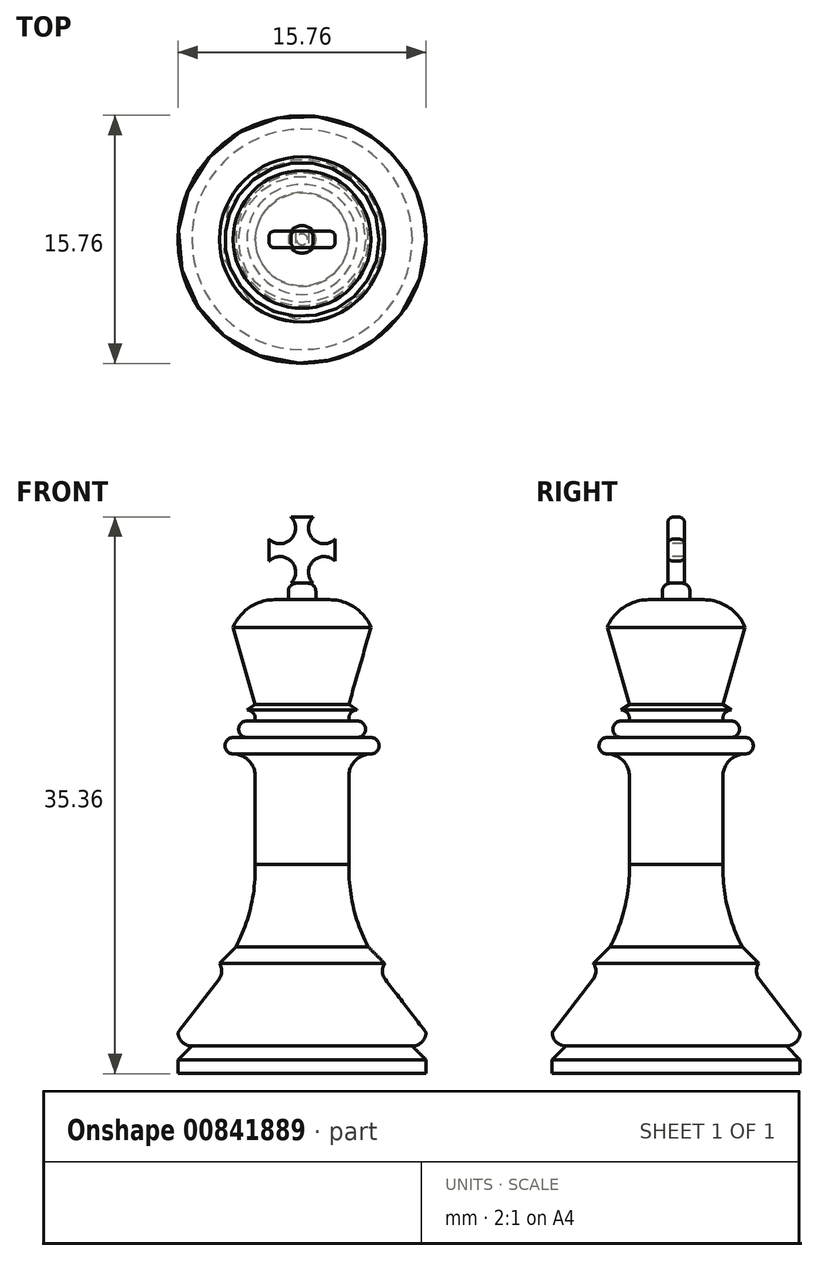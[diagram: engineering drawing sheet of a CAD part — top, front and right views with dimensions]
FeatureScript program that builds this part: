
annotation { "Feature Type Name" : "Feature", "Feature Type Description" : "" }
export const myFeature = defineFeature(function(context is Context, id is Id, definition is map)
    precondition{}
    {
        {
            var Q0;
            Q0=qCreatedBy(makeId("Front.planeOp"),FACE);
            var sketch = newSketch(context, id + "F0", { "sketchPlane" : qUnion([Q0])});
            skLineSegment(sketch, "E0", {"start": v(0, 0) * mm, "end": v(0, 33.5) * mm});
            skLineSegment(sketch, "E1", {"start": v(0, 0) * mm, "end": v(0, -52.5) * mm});
            skLineSegment(sketch, "E2", {"start": v(0, -52.5) * mm, "end": v(-22.5, -52.5) * mm});
            skLineSegment(sketch, "E3", {"start": v(-22.5, -52.5) * mm, "end": v(-22.5, -50) * mm});
            skLineSegment(sketch, "E4", {"start": v(-15, -32.5) * mm, "end": v(-15, -32.5) * mm});
            skLineSegment(sketch, "E5", {"start": v(-22.5, -50) * mm, "end": v(-20, -47.5) * mm});
            skLineSegment(sketch, "E6", {"start": v(-22.5, -45) * mm, "end": v(-22.5, -45) * mm});
            skLineSegment(sketch, "E7", {"start": v(-20, -47.5) * mm, "end": v(-20, -47.5) * mm});
            skPoint(sketch, "E8.visualSharp", {"position": v(-22.5, -47.5) * mm});
            skArc(sketch, "E8.filletArc", {"start": v(-22.47, -45.4) * mm, "mid": v(-21.62, -46.9) * mm, "end": v(-20, -47.5) * mm});
            skLineSegment(sketch, "E9", {"start": v(-15.1, -35.42) * mm, "end": v(-22.3, -44.74) * mm});
            skPoint(sketch, "E10.visualSharp", {"position": v(-22.5, -45) * mm});
            skArc(sketch, "E10.filletArc", {"start": v(-22.3, -44.74) * mm, "mid": v(-22.45, -45.05) * mm, "end": v(-22.47, -45.4) * mm});
            skPoint(sketch, "E11.visualSharp", {"position": v(-14, -34) * mm});
            skArc(sketch, "E11.filletArc", {"start": v(-15.1, -35.42) * mm, "mid": v(-14.58, -33.98) * mm, "end": v(-15, -32.5) * mm});
            skLineSegment(sketch, "E12", {"start": v(-12, -29.5) * mm, "end": v(-15, -32.5) * mm});
            skArc(sketch, "E13", {"start": v(-12, -29.5) * mm, "mid": v(-9.3, -22.22) * mm, "end": v(-8.5, -14.5) * mm});
            skLineSegment(sketch, "E14", {"start": v(-8.5, 1.5) * mm, "end": v(-8.5, -14.5) * mm});
            skLineSegment(sketch, "E15", {"start": v(-12.5, 5.5) * mm, "end": v(-12.5, 5.5) * mm});
            skLineSegment(sketch, "E16", {"start": v(0, 8.5) * mm, "end": v(-12.5, 8.5) * mm});
            skArc(sketch, "E17", {"start": v(-12.5, 8.5) * mm, "mid": v(-14, 7) * mm, "end": v(-12.5, 5.5) * mm});
            skLineSegment(sketch, "E18", {"start": v(-15, -32.5) * mm, "end": v(0, -32.5) * mm});
            skLineSegment(sketch, "E19", {"start": v(-20, -47.5) * mm, "end": v(0, -47.5) * mm});
            skLineSegment(sketch, "E20", {"start": v(0, 8.5) * mm, "end": v(-10, 8.5) * mm});
            skLineSegment(sketch, "E21", {"start": v(-8.5, 11.5) * mm, "end": v(-10, 11.5) * mm});
            skArc(sketch, "E22", {"start": v(-10, 11.5) * mm, "mid": v(-11.5, 10) * mm, "end": v(-10, 8.5) * mm});
            skLineSegment(sketch, "E23", {"start": v(-8.5, 11.5) * mm, "end": v(-8.5, 12) * mm});
            skLineSegment(sketch, "E24", {"start": v(-10, 13.5) * mm, "end": v(-10, 13.5) * mm});
            skLineSegment(sketch, "E25", {"start": v(-10, 13.5) * mm, "end": v(-8.5, 14.5) * mm});
            skLineSegment(sketch, "E26", {"start": v(-8.5, 14.5) * mm, "end": v(0, 14.5) * mm});
            skLineSegment(sketch, "E27", {"start": v(-12.5, 28.5) * mm, "end": v(-8.5, 14.5) * mm});
            skLineSegment(sketch, "E28", {"start": v(0, 33.5) * mm, "end": v(-5, 33.5) * mm});
            skArc(sketch, "E29", {"start": v(-5, 33.5) * mm, "mid": v(-9.5, 32.14) * mm, "end": v(-12.5, 28.5) * mm});
            skPoint(sketch, "E30.newPointB", {"position": v(0, 5.5) * mm});
            skArc(sketch, "E30.filletArc", {"start": v(-8.5, 1.5) * mm, "mid": v(-9.67, 4.33) * mm, "end": v(-12.5, 5.5) * mm});
            skPoint(sketch, "E31.end.orphan", {"position": v(-8.5, 5.5) * mm});
            skPoint(sketch, "E32.visualSharp", {"position": v(-8.5, 13.5) * mm});
            skArc(sketch, "E32.filletArc", {"start": v(-8.5, 12) * mm, "mid": v(-8.94, 13.06) * mm, "end": v(-10, 13.5) * mm});
            skPoint(sketch, "E33.end.orphan", {"position": v(0, 13.5) * mm});
            skSolve(sketch);
        }
        {
            var Q0;
            Q0 = qSketchRegion(id + "F0", true);
            var Q1;
            Q1=sQuery(id+"F0.wireOp",EDGE,"E1");
            revolve(context, id + "F1", {"surfaceOperationType" : NewSurfaceOperationType.NEW, "entities" : qUnion([Q0]), "axis" : qUnion([Q1]), "revolveType" : RevolveType.FULL});
        }
        {
            var Q0;
            Q0=makeQuery(id+"F1.opRevolve","SWEPT_FACE",FACE,{"disambiguationData":[OSD([sQuery(id+"F0.wireOp",EDGE,"E28")])]});
            var sketch = newSketch(context, id + "F2", { "sketchPlane" : qUnion([Q0])});
            skCircle(sketch, "E34", {"center": v(0, 0) * mm, "radius": 2.5 * mm});
            skSolve(sketch);
        }
        {
            var Q0;
            Q0 = qSketchRegion(id + "F2", true);
            extrude(context, id + "F3", {"entities" : qUnion([Q0]), "operationType" : NewBodyOperationType.ADD, "depth" : 3 * mm, "offsetDistance" : 25 * mm});
        }
        {
            var Q0;
            Q0=makeQuery(id+"F3.opExtrude","CAP_EDGE",EDGE,{"disambiguationData":[OSD([sQuery(id+"F2.wireOp",EDGE,"E34")])],"isStart":false});
            fillet(context, id + "F4", {"entities" : qUnion([Q0]), "radius" : 1.5 * mm, "tangentPropagation" : true, "allowEdgeOverflow" : false});
        }
        {
            var Q0;
            Q0=makeQuery(id+"F3.opExtrude","CAP_FACE",FACE,{"disambiguationData":[OSD([sQuery(id+"F2.wireOp",EDGE,"E34")])],"isStart":false});
            var sketch = newSketch(context, id + "F5", { "sketchPlane" : qUnion([Q0])});
            skLineSegment(sketch, "E35.bottom", {"start": v(-6, 1.5) * mm, "end": v(6, 1.5) * mm});
            skLineSegment(sketch, "E35.top", {"start": v(-6, -1.5) * mm, "end": v(6, -1.5) * mm});
            skLineSegment(sketch, "E35.left", {"start": v(-6, 1.5) * mm, "end": v(-6, -1.5) * mm});
            skLineSegment(sketch, "E35.right", {"start": v(6, 1.5) * mm, "end": v(6, -1.5) * mm});
            skPoint(sketch, "E35.middle", {"position": v(0, 0) * mm});
            skSolve(sketch);
        }
        {
            var Q0;
            Q0 = qSketchRegion(id + "F5", true);
            extrude(context, id + "F6", {"entities" : qUnion([Q0]), "operationType" : NewBodyOperationType.ADD, "depth" : 12 * mm, "offsetDistance" : 25 * mm});
        }
        {
            var Q0;
            Q0=makeQuery(id+"F6.opExtrude","SWEPT_FACE",FACE,{"disambiguationData":[OSD([sQuery(id+"F5.wireOp",EDGE,"E35.top")])]});
            var sketch = newSketch(context, id + "F7", { "sketchPlane" : qUnion([Q0])});
            skPoint(sketch, "E36.middle", {"position": v(0, 42.5) * mm});
            skCircle(sketch, "E37", {"center": v(-4, 46.5) * mm, "radius": 2.83 * mm});
            skCircle(sketch, "E38", {"center": v(4, 46.5) * mm, "radius": 2.83 * mm});
            skCircle(sketch, "E39", {"center": v(4, 38.5) * mm, "radius": 2.83 * mm});
            skCircle(sketch, "E40", {"center": v(-4, 38.5) * mm, "radius": 2.83 * mm});
            skSolve(sketch);
        }
        {
            var Q0;
            Q0 = qSketchRegion(id + "F7", true);
            extrude(context, id + "F8", {"entities" : qUnion([Q0]), "operationType" : NewBodyOperationType.REMOVE, "oppositeDirection" : true, "depth" : 3 * mm, "offsetDistance" : 25 * mm});
        }
        {
            var Q0;
            Q0=makeQuery(id+"F8.boolean.opBoolean","COPY",EDGE,{"derivedFrom":makeQuery(id+"F8.opExtrude","CAP_EDGE",EDGE,{"disambiguationData":[OSD([sQuery(id+"F7.wireOp",EDGE,"E37")])],"isStart":true})});
            var Q1;
            Q1=makeQuery(id+"F6.opExtrude","CAP_EDGE",EDGE,{"disambiguationData":[OSD([sQuery(id+"F5.wireOp",EDGE,"E35.top")])],"isStart":false});
            var Q2;
            Q2=makeQuery(id+"F8.boolean.opBoolean","COPY",EDGE,{"derivedFrom":makeQuery(id+"F8.opExtrude","CAP_EDGE",EDGE,{"disambiguationData":[OSD([sQuery(id+"F7.wireOp",EDGE,"E38")])],"isStart":true})});
            var Q3;
            Q3=makeQuery(id+"F6.opExtrude","SWEPT_EDGE",EDGE,{"disambiguationData":[OSD([sQuery(id+"F5.wireOp",EDGE,"E35.top"),sQuery(id+"F5.wireOp",EDGE,"E35.right")])]});
            var Q4;
            Q4=makeQuery(id+"F8.boolean.opBoolean","COPY",EDGE,{"derivedFrom":makeQuery(id+"F8.opExtrude","CAP_EDGE",EDGE,{"disambiguationData":[OSD([sQuery(id+"F7.wireOp",EDGE,"E39")])],"isStart":true})});
            var Q5;
            Q5=makeQuery(id+"F8.boolean.opBoolean","COPY",EDGE,{"derivedFrom":makeQuery(id+"F8.opExtrude","CAP_EDGE",EDGE,{"disambiguationData":[OSD([sQuery(id+"F7.wireOp",EDGE,"E40")])],"isStart":true})});
            var Q6;
            Q6=makeQuery(id+"F6.opExtrude","SWEPT_EDGE",EDGE,{"disambiguationData":[OSD([sQuery(id+"F5.wireOp",EDGE,"E35.top"),sQuery(id+"F5.wireOp",EDGE,"E35.left")])]});
            fillet(context, id + "F9", {"entities" : qUnion([Q0, Q1, Q2, Q3, Q4, Q5, Q6]), "radius" : 1 * mm, "tangentPropagation" : true, "allowEdgeOverflow" : false});
        }
        {
            var Q0;
            Q0=makeQuery(id+"F8.boolean.opBoolean","COPY",EDGE,{"derivedFrom":makeQuery(id+"F8.opExtrude","CAP_EDGE",EDGE,{"disambiguationData":[OSD([sQuery(id+"F7.wireOp",EDGE,"E38")])],"isStart":false})});
            var Q1;
            Q1=makeQuery(id+"F6.opExtrude","SWEPT_EDGE",EDGE,{"disambiguationData":[OSD([sQuery(id+"F5.wireOp",EDGE,"E35.bottom"),sQuery(id+"F5.wireOp",EDGE,"E35.right")])]});
            var Q2;
            Q2=makeQuery(id+"F8.boolean.opBoolean","COPY",EDGE,{"derivedFrom":makeQuery(id+"F8.opExtrude","CAP_EDGE",EDGE,{"disambiguationData":[OSD([sQuery(id+"F7.wireOp",EDGE,"E39")])],"isStart":false})});
            var Q3;
            Q3=makeQuery(id+"F8.boolean.opBoolean","COPY",EDGE,{"derivedFrom":makeQuery(id+"F8.opExtrude","CAP_EDGE",EDGE,{"disambiguationData":[OSD([sQuery(id+"F7.wireOp",EDGE,"E40")])],"isStart":false})});
            var Q4;
            Q4=makeQuery(id+"F6.opExtrude","SWEPT_EDGE",EDGE,{"disambiguationData":[OSD([sQuery(id+"F5.wireOp",EDGE,"E35.bottom"),sQuery(id+"F5.wireOp",EDGE,"E35.left")])]});
            var Q5;
            Q5=makeQuery(id+"F8.boolean.opBoolean","COPY",EDGE,{"derivedFrom":makeQuery(id+"F8.opExtrude","CAP_EDGE",EDGE,{"disambiguationData":[OSD([sQuery(id+"F7.wireOp",EDGE,"E37")])],"isStart":false})});
            var Q6;
            Q6=makeQuery(id+"F6.opExtrude","CAP_EDGE",EDGE,{"disambiguationData":[OSD([sQuery(id+"F5.wireOp",EDGE,"E35.bottom")])],"isStart":false});
            fillet(context, id + "F10", {"entities" : qUnion([Q0, Q1, Q2, Q3, Q4, Q5, Q6]), "radius" : 1 * mm, "tangentPropagation" : true, "allowEdgeOverflow" : false});
        }
        {
            var Q0;
            Q0=makeQuery(id+"F1.opRevolve","SWEPT_BODY",BODY,{"disambiguationData":[OSD([sQuery(id+"F0.wireOp",EDGE,"E0"),sQuery(id+"F0.wireOp",EDGE,"E1"),sQuery(id+"F0.wireOp",EDGE,"E2"),sQuery(id+"F0.wireOp",EDGE,"E3"),sQuery(id+"F0.wireOp",EDGE,"E4"),sQuery(id+"F0.wireOp",EDGE,"E5"),sQuery(id+"F0.wireOp",EDGE,"E8.filletArc"),sQuery(id+"F0.wireOp",EDGE,"E9"),sQuery(id+"F0.wireOp",EDGE,"E10.filletArc"),sQuery(id+"F0.wireOp",EDGE,"E4"),sQuery(id+"F0.wireOp",EDGE,"E11.filletArc"),sQuery(id+"F0.wireOp",EDGE,"E12"),sQuery(id+"F0.wireOp",EDGE,"E13"),sQuery(id+"F0.wireOp",EDGE,"E14"),sQuery(id+"F0.wireOp",EDGE,"E15"),sQuery(id+"F0.wireOp",EDGE,"E16"),sQuery(id+"F0.wireOp",EDGE,"E17"),sQuery(id+"F0.wireOp",EDGE,"E21"),sQuery(id+"F0.wireOp",EDGE,"E22"),sQuery(id+"F0.wireOp",EDGE,"E23"),sQuery(id+"F0.wireOp",EDGE,"E24"),sQuery(id+"F0.wireOp",EDGE,"E25"),sQuery(id+"F0.wireOp",EDGE,"E27"),sQuery(id+"F0.wireOp",EDGE,"E28"),sQuery(id+"F0.wireOp",EDGE,"E29")])]});
            var Q1;
            Q1=qCreatedBy(makeId("Origin.pointOp"),VERTEX);
            transform(context, id + "F11", {"entities" : qUnion([Q0]), "transformType" : TransformType.SCALE_UNIFORMLY, "scale" : 0.35, "scalePoint" : qUnion([Q1]), "makeCopy" : false});
        }
    });
